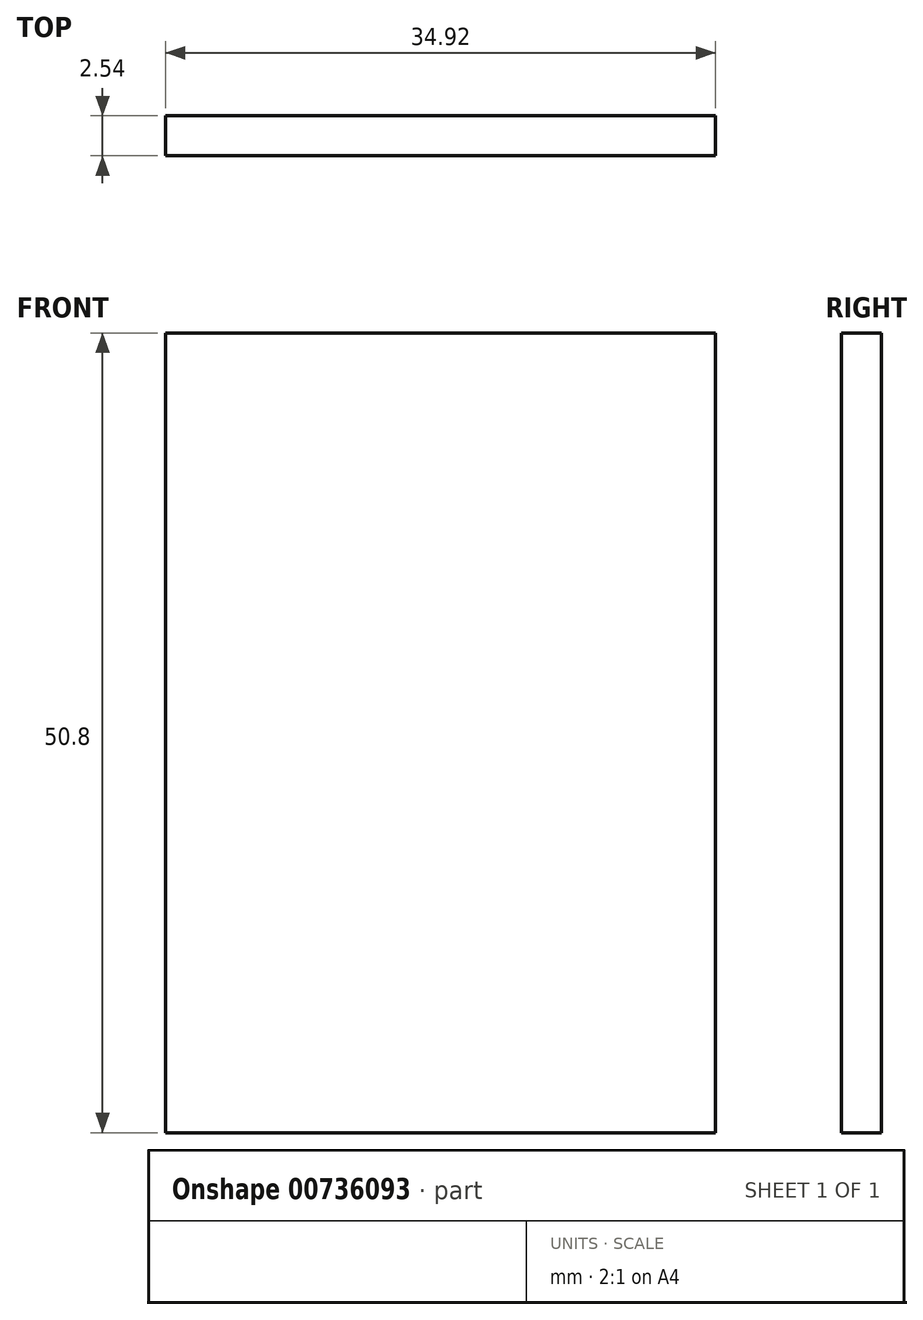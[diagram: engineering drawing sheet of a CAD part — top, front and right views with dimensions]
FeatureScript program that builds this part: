
annotation { "Feature Type Name" : "Feature", "Feature Type Description" : "" }
export const myFeature = defineFeature(function(context is Context, id is Id, definition is map)
    precondition{}
    {
        {
            var Q0;
            Q0=qCreatedBy(makeId("Top.planeOp"),FACE);
            var sketch = newSketch(context, id + "F0", { "sketchPlane" : qUnion([Q0])});
            skLineSegment(sketch, "E0.bottom", {"start": v(-4.63, 40.75) * mm, "end": v(35.37, 40.75) * mm});
            skLineSegment(sketch, "E0.top", {"start": v(-4.63, -35.45) * mm, "end": v(35.37, -35.45) * mm});
            skLineSegment(sketch, "E0.left", {"start": v(-4.63, 40.75) * mm, "end": v(-4.63, -35.45) * mm});
            skLineSegment(sketch, "E0.right", {"start": v(35.37, 40.75) * mm, "end": v(35.37, -35.45) * mm});
            skLineSegment(sketch, "E1", {"start": v(35.37, -35.45) * mm, "end": v(35.37, -32.91) * mm});
            skLineSegment(sketch, "E2", {"start": v(35.37, -35.45) * mm, "end": v(32.83, -35.45) * mm});
            skLineSegment(sketch, "E3", {"start": v(-4.63, -35.45) * mm, "end": v(-2.1, -35.45) * mm});
            skLineSegment(sketch, "E4", {"start": v(35.37, 40.75) * mm, "end": v(32.83, 40.75) * mm});
            skLineSegment(sketch, "E5", {"start": v(35.37, 40.75) * mm, "end": v(35.37, 38.2) * mm});
            skLineSegment(sketch, "E6", {"start": v(-4.63, 40.75) * mm, "end": v(-2.1, 40.75) * mm});
            skLineSegment(sketch, "E7", {"start": v(-4.63, 40.75) * mm, "end": v(-4.63, 38.2) * mm});
            skPoint(sketch, "E8.end.orphan", {"position": v(-4.63, -36.4) * mm});
            skLineSegment(sketch, "E9", {"start": v(-2.1, 40.75) * mm, "end": v(-2.1, -35.45) * mm});
            skLineSegment(sketch, "E10", {"start": v(32.83, -35.45) * mm, "end": v(32.83, 40.75) * mm});
            skLineSegment(sketch, "E11", {"start": v(-4.63, 38.2) * mm, "end": v(35.37, 38.2) * mm});
            skLineSegment(sketch, "E12", {"start": v(35.37, -32.91) * mm, "end": v(-4.63, -32.91) * mm});
            skSolve(sketch);
        }
        {
            var Q0;
            {var subQ0=sQuery(id+"F0.wireOp",EDGE,"E9");var subQ1=sQuery(id+"F0.wireOp",EDGE,"E0.bottom");var subQ2=makeQuery(id+"F0.imprint","INTERSECT",VERTEX,{"derivedFrom":[subQ1,subQ0]});Q0=makeQuery(id+"F0.imprint","IMPRINT",FACE,{"disambiguationData":[TD([[makeQuery(id+"F0.imprint","IMPRINT",EDGE,{"disambiguationData":[TD([[subQ2,-1.0]])],"derivedFrom":subQ1}),-1.0]])]});}
            extrude(context, id + "F1", {"entities" : qUnion([Q0]), "depth" : 50.8 * mm, "offsetDistance" : 25.4 * mm});
        }
    });
